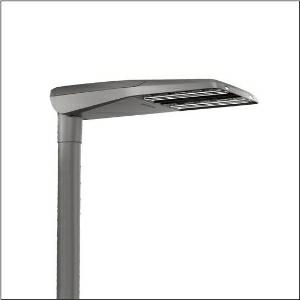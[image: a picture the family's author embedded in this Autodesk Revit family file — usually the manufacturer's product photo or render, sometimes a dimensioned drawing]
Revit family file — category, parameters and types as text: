
# Revit family: streetlight_sl_11_iq_midi___st1_2a_5xc3a41e08le_4284
name_source: partatom
category: Lighting Fixtures
units: mm (PartAtom-declared; Revit-internal decimal feet)

## family parameters
Cut with Voids When Loaded = No
Host = Face
Light Source = No
Part Type = Normal
Room Calculation Point = No
Round Connector Dimension = Use Diameter
Shared = No

## types (1)
- --- (1 x LED, 9590 lm, 60.4 W, 4000K)
    Apparent Load = 60 VA
    CIE Flux Codes = 32 70 96 100 100
    Color Rendering = 70
    Color Temperature = 4000K
    Default Elevation = 1800 mm
    Description = Streetlight SL 11 iQ midi, mast luminaire, primary light control with 3 zone facetted reflector, of plastic, silver coated, highly specular, primary optical cover: cover, of PMMA, transparent, light distribution: ST1.2a, light emission: direct distribution, primary light characteristic: asymmetric, installation type: post-top, side-entry, LED, High Power LED, rated luminous flux: 9.590lm, luminous efficacy: 159lm/W, light colour: 740, colour temperature: 4000K, control: optimised constant luminous flux control (CLO 2.0), Desk-Remote (wireless, voltage-free reading and setting of iQ features in the workshop via application-optimized NFC function/RFID function), Light-Fading, Smart-Wire, Night-Set, Lumen-Switch, Temp-Guard, Auto-Match, with cable H07RN-F 5x 1.5mm², mains connection: 220..240V, AC, 50/60Hz, connection cable pre-assembled, cable length: 8,5m, start of lifetime: 60W, end of lifetime: 63W, reduction: 30W, luminaire housing, of diecast aluminium, powder-coated, Siteco® metallic grey (DB 702S), length: 780mm, width: 376mm, height: 118mm, spigot size: 60/76mm (post-top) and 42/60/76mm (side-entry), mast flange for spigot size: 42mm: 5XC10008XM4, 60mm: 5XC10008XM2, 76/60mm: 5XC10108XM1, equipment: standard, protection rating (complete): IP66, insulation class (complete): insulation class II (safety insulation), certification: CE, ENEC, VDE, impact resistance: IK09, permissible operating ambient temperature for outdoor applications: -25..+50°C, standard-compliant lighting for roads and squares, packaging unit: 1 piece

Light Distribution: ST1.2a
    Height = 118 mm
    Lamp = 1 x LED
    Lamp Light Flux = 9590 lm
    Lamp Power = 60.4 W
    Lamp count = 1
    Length = 780 mm
    Luminous efficacy = 159 lm/W
    Manufacturer = Siteco
    ModVariant = No
    Model = 5XC3A41E08LE
    Number of Poles = 1
    OnlyDefault = Yes
    Power Factor = 1
    Product Name = Streetlight SL 11 iQ midi | ST1.2a
    Product group = mast luminaire | pylon top
    ProductGroupID = 6100
    Protection Class = Protection class II
    Protection Degree = IP 66
    RLX_Detail_Level = 1
    RlxData = <blob elided: 70297 chars, md5=fc962a29>
    Socket = socket
    Standby Power = 0 W
    System Light Flux = 9590 lm
    System Power = 60 W
    Type Comments = factory setting: luminous flux: 100 % | dim-lin: 254 | 520 mA
    Type Image = l_1005960.jpg
    URL = http://relux.com
    VarID = @adj_120847
    Voltage = 0 V
    Weight = 0.00 kg
    Width = 376 mm

## geometry (parser evidence)
native form markers: Blend x4, Sweep x12
no freeform markers — native parametric forms only
